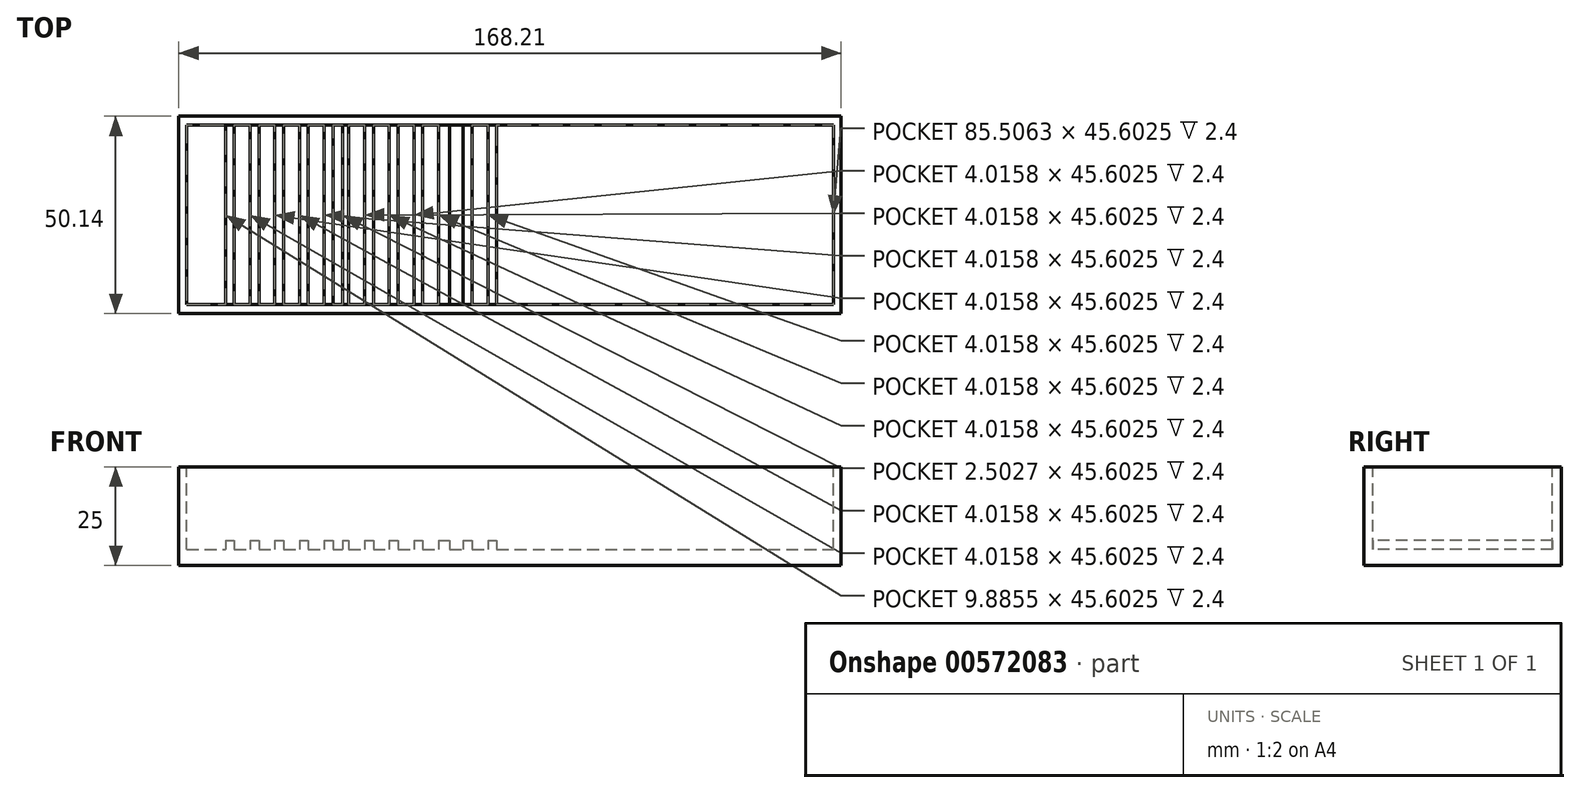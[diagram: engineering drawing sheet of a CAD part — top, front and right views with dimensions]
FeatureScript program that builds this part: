
annotation { "Feature Type Name" : "Feature", "Feature Type Description" : "" }
export const myFeature = defineFeature(function(context is Context, id is Id, definition is map)
    precondition{}
    {
        {
            var Q0;
            Q0=qCreatedBy(makeId("Top.planeOp"),FACE);
            var sketch = newSketch(context, id + "F0", { "sketchPlane" : qUnion([Q0])});
            skLineSegment(sketch, "E0.bottom", {"start": v(-65.98, 17.93) * mm, "end": v(102.23, 17.93) * mm});
            skLineSegment(sketch, "E0.top", {"start": v(-65.98, -32.21) * mm, "end": v(102.23, -32.21) * mm});
            skLineSegment(sketch, "E0.left", {"start": v(-65.98, 17.93) * mm, "end": v(-65.98, -32.21) * mm});
            skLineSegment(sketch, "E0.right", {"start": v(102.23, 17.93) * mm, "end": v(102.23, -32.21) * mm});
            skSolve(sketch);
        }
        {
            var Q0;
            Q0=makeQuery(id+"F0.imprint","IMPRINT",FACE,{"disambiguationData":[TD([[makeQuery(id+"F0.imprint","IMPRINT",EDGE,{"derivedFrom":sQuery(id+"F0.wireOp",EDGE,"E0.bottom")}),-1.0]])]});
            extrude(context, id + "F1", {"entities" : qUnion([Q0]), "depth" : 25 * mm, "offsetDistance" : 25 * mm});
        }
        {
            var Q0;
            Q0=makeQuery(id+"F1.opExtrude","CAP_FACE",FACE,{"disambiguationData":[OSD([sQuery(id+"F0.wireOp",EDGE,"E0.bottom"),sQuery(id+"F0.wireOp",EDGE,"E0.top"),sQuery(id+"F0.wireOp",EDGE,"E0.left"),sQuery(id+"F0.wireOp",EDGE,"E0.right")])],"isStart":false});
            var sketch = newSketch(context, id + "F2", { "sketchPlane" : qUnion([Q0])});
            skLineSegment(sketch, "E1.bottom", {"start": v(-64.01, 15.66) * mm, "end": v(100.27, 15.66) * mm});
            skLineSegment(sketch, "E1.top", {"start": v(-64.01, -29.94) * mm, "end": v(100.27, -29.94) * mm});
            skLineSegment(sketch, "E1.left", {"start": v(-64.01, 15.66) * mm, "end": v(-64.01, -29.94) * mm});
            skLineSegment(sketch, "E1.right", {"start": v(100.27, 15.66) * mm, "end": v(100.27, -29.94) * mm});
            skSolve(sketch);
        }
        {
            var Q0;
            Q0=makeQuery(id+"F2.imprint","IMPRINT",FACE,{"disambiguationData":[TD([[makeQuery(id+"F2.imprint","IMPRINT",EDGE,{"derivedFrom":sQuery(id+"F2.wireOp",EDGE,"E1.bottom")}),-1.0]])]});
            extrude(context, id + "F3", {"entities" : qUnion([Q0]), "operationType" : NewBodyOperationType.REMOVE, "oppositeDirection" : true, "depth" : 21 * mm, "offsetDistance" : 25 * mm});
        }
        {
            var Q0;
            Q0=makeQuery(id+"F3.boolean.opBoolean","COPY",FACE,{"derivedFrom":makeQuery(id+"F3.opExtrude","CAP_FACE",FACE,{"disambiguationData":[OSD([sQuery(id+"F2.wireOp",EDGE,"E1.bottom"),sQuery(id+"F2.wireOp",EDGE,"E1.top"),sQuery(id+"F2.wireOp",EDGE,"E1.left"),sQuery(id+"F2.wireOp",EDGE,"E1.right")])],"isStart":false})});
            var sketch = newSketch(context, id + "F4", { "sketchPlane" : qUnion([Q0])});
            skLineSegment(sketch, "E2.bottom", {"start": v(-54.13, 15.66) * mm, "end": v(-51.9, 15.66) * mm});
            skLineSegment(sketch, "E2.top", {"start": v(-54.13, -29.94) * mm, "end": v(-51.9, -29.94) * mm});
            skLineSegment(sketch, "E2.left", {"start": v(-54.13, 15.66) * mm, "end": v(-54.13, -29.94) * mm});
            skLineSegment(sketch, "E2.right", {"start": v(-51.9, 15.66) * mm, "end": v(-51.9, -29.94) * mm});
            skLineSegment(sketch, "E3.bottom", {"start": v(-41.6, 15.66) * mm, "end": v(-39.36, 15.66) * mm});
            skLineSegment(sketch, "E3.top", {"start": v(-41.6, -29.94) * mm, "end": v(-39.36, -29.94) * mm});
            skLineSegment(sketch, "E3.left", {"start": v(-41.6, 15.66) * mm, "end": v(-41.6, -29.94) * mm});
            skLineSegment(sketch, "E3.right", {"start": v(-39.36, 15.66) * mm, "end": v(-39.36, -29.94) * mm});
            skLineSegment(sketch, "E4.bottom", {"start": v(-29.07, 15.66) * mm, "end": v(-26.84, 15.66) * mm});
            skLineSegment(sketch, "E4.top", {"start": v(-29.07, -29.94) * mm, "end": v(-26.84, -29.94) * mm});
            skLineSegment(sketch, "E4.left", {"start": v(-29.07, 15.66) * mm, "end": v(-29.07, -29.94) * mm});
            skLineSegment(sketch, "E4.right", {"start": v(-26.84, 15.66) * mm, "end": v(-26.84, -29.94) * mm});
            skLineSegment(sketch, "E5.bottom", {"start": v(-18.78, 15.66) * mm, "end": v(-16.54, 15.66) * mm});
            skLineSegment(sketch, "E5.top", {"start": v(-18.78, -29.94) * mm, "end": v(-16.54, -29.94) * mm});
            skLineSegment(sketch, "E5.left", {"start": v(-16.54, 15.66) * mm, "end": v(-16.54, -29.94) * mm});
            skLineSegment(sketch, "E5.right", {"start": v(-18.78, 15.66) * mm, "end": v(-18.78, -29.94) * mm});
            skLineSegment(sketch, "E6.bottom", {"start": v(-6.25, 15.66) * mm, "end": v(-4.02, 15.66) * mm});
            skLineSegment(sketch, "E6.top", {"start": v(-6.25, -29.94) * mm, "end": v(-4.02, -29.94) * mm});
            skLineSegment(sketch, "E6.left", {"start": v(-6.25, 15.66) * mm, "end": v(-6.25, -29.94) * mm});
            skLineSegment(sketch, "E6.right", {"start": v(-4.02, 15.66) * mm, "end": v(-4.02, -29.94) * mm});
            skLineSegment(sketch, "E7.bottom", {"start": v(6.28, 15.66) * mm, "end": v(8.51, 15.66) * mm});
            skLineSegment(sketch, "E7.top", {"start": v(6.28, -29.94) * mm, "end": v(8.51, -29.94) * mm});
            skLineSegment(sketch, "E7.left", {"start": v(6.28, 15.66) * mm, "end": v(6.28, -29.94) * mm});
            skLineSegment(sketch, "E7.right", {"start": v(8.51, 15.66) * mm, "end": v(8.51, -29.94) * mm});
            skLineSegment(sketch, "E8.bottom", {"start": v(-47.88, 15.66) * mm, "end": v(-45.62, 15.66) * mm});
            skLineSegment(sketch, "E8.top", {"start": v(-47.88, -29.94) * mm, "end": v(-45.62, -29.94) * mm});
            skLineSegment(sketch, "E8.left", {"start": v(-47.88, 15.66) * mm, "end": v(-47.88, -29.94) * mm});
            skLineSegment(sketch, "E8.right", {"start": v(-45.62, 15.66) * mm, "end": v(-45.62, -29.94) * mm});
            skLineSegment(sketch, "E9.bottom", {"start": v(-35.35, 15.66) * mm, "end": v(-33.09, 15.66) * mm});
            skLineSegment(sketch, "E9.top", {"start": v(-35.35, -29.94) * mm, "end": v(-33.09, -29.94) * mm});
            skLineSegment(sketch, "E9.left", {"start": v(-35.35, 15.66) * mm, "end": v(-35.35, -29.94) * mm});
            skLineSegment(sketch, "E9.right", {"start": v(-33.09, 15.66) * mm, "end": v(-33.09, -29.94) * mm});
            skLineSegment(sketch, "E10.bottom", {"start": v(-24.33, 15.66) * mm, "end": v(-22.8, 15.66) * mm});
            skLineSegment(sketch, "E10.top", {"start": v(-24.33, -29.94) * mm, "end": v(-22.8, -29.94) * mm});
            skLineSegment(sketch, "E10.left", {"start": v(-24.33, 15.66) * mm, "end": v(-24.33, -29.94) * mm});
            skLineSegment(sketch, "E10.right", {"start": v(-22.8, 15.66) * mm, "end": v(-22.8, -29.94) * mm});
            skLineSegment(sketch, "E11.bottom", {"start": v(-12.53, 15.66) * mm, "end": v(-10.27, 15.66) * mm});
            skLineSegment(sketch, "E11.top", {"start": v(-12.53, -29.94) * mm, "end": v(-10.27, -29.94) * mm});
            skLineSegment(sketch, "E11.left", {"start": v(-12.53, 15.66) * mm, "end": v(-12.53, -29.94) * mm});
            skLineSegment(sketch, "E11.right", {"start": v(-10.27, 15.66) * mm, "end": v(-10.27, -29.94) * mm});
            skLineSegment(sketch, "E12.bottom", {"start": v(2.8, 15.66) * mm, "end": v(0, 15.66) * mm});
            skLineSegment(sketch, "E12.top", {"start": v(2.8, -29.94) * mm, "end": v(0, -29.94) * mm});
            skLineSegment(sketch, "E12.left", {"start": v(2.8, 15.66) * mm, "end": v(2.8, -29.94) * mm});
            skLineSegment(sketch, "E12.right", {"start": v(0, 15.66) * mm, "end": v(0, -29.94) * mm});
            skLineSegment(sketch, "E13.bottom", {"start": v(12.53, 15.66) * mm, "end": v(14.77, 15.66) * mm});
            skLineSegment(sketch, "E13.top", {"start": v(12.53, -29.94) * mm, "end": v(14.77, -29.94) * mm});
            skLineSegment(sketch, "E13.left", {"start": v(12.53, 15.66) * mm, "end": v(12.53, -29.94) * mm});
            skLineSegment(sketch, "E13.right", {"start": v(14.77, 15.66) * mm, "end": v(14.77, -29.94) * mm});
            skSolve(sketch);
        }
        {
            var Q0;
            Q0 = qSketchRegion(id + "F4", true);
            extrude(context, id + "F5", {"entities" : qUnion([Q0]), "operationType" : NewBodyOperationType.ADD, "depth" : 2.4 * mm, "offsetDistance" : 25 * mm});
        }
    });
